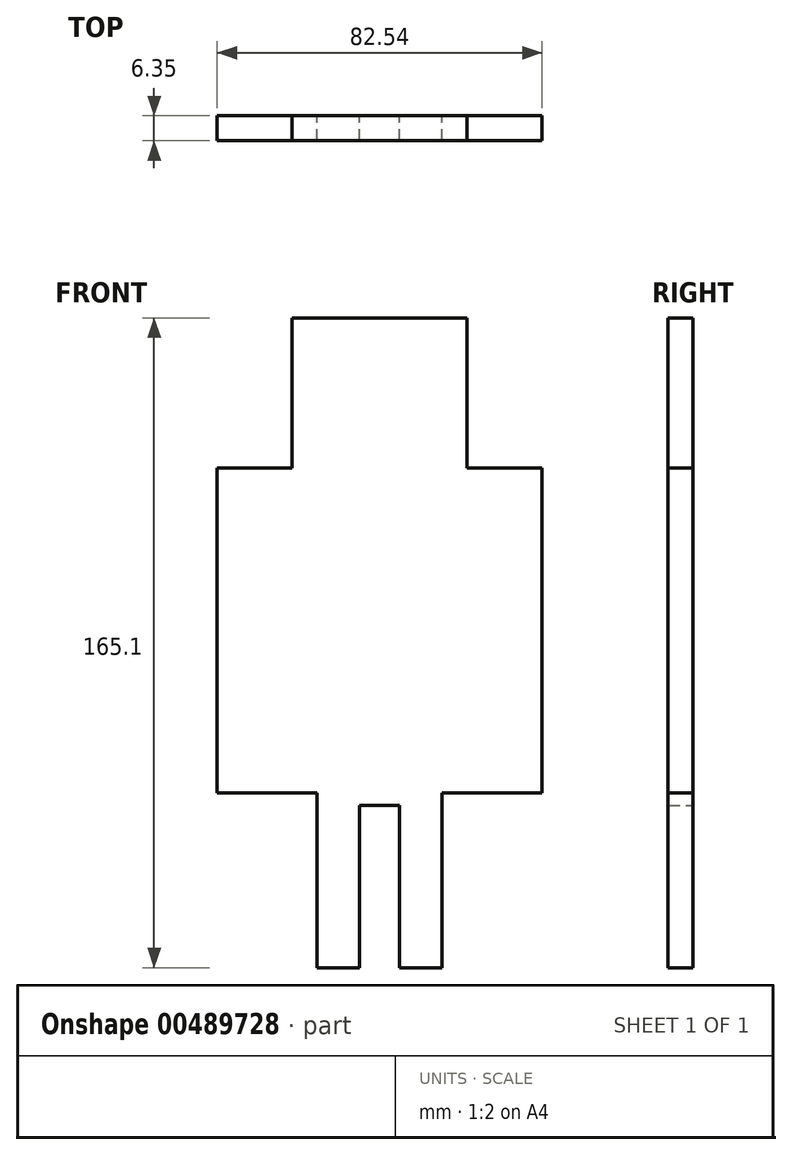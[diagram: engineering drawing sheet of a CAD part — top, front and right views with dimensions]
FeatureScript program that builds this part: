
annotation { "Feature Type Name" : "Feature", "Feature Type Description" : "" }
export const myFeature = defineFeature(function(context is Context, id is Id, definition is map)
    precondition{}
    {
        {
            var Q0;
            Q0=qCreatedBy(makeId("Front.planeOp"),FACE);
            var sketch = newSketch(context, id + "F0", { "sketchPlane" : qUnion([Q0])});
            skLineSegment(sketch, "E0.bottom", {"start": v(-22.23, 82.55) * mm, "end": v(22.23, 82.55) * mm});
            skLineSegment(sketch, "E0.top", {"start": v(-15.88, -82.55) * mm, "end": v(-5.08, -82.55) * mm});
            skLineSegment(sketch, "E0.left", {"start": v(-41.28, 44.45) * mm, "end": v(-41.28, -38.1) * mm});
            skLineSegment(sketch, "E0.right", {"start": v(41.28, 44.45) * mm, "end": v(41.28, -38.1) * mm});
            skLineSegment(sketch, "E1.bottom", {"start": v(-41.28, 44.45) * mm, "end": v(-41.28, 44.45) * mm});
            skLineSegment(sketch, "E2.MirrorCS", {"start": v(41.28, 44.45) * mm, "end": v(41.28, 44.45) * mm});
            skLineSegment(sketch, "E3.bottom", {"start": v(-41.28, -38.1) * mm, "end": v(-15.88, -38.1) * mm});
            skLineSegment(sketch, "E3.right", {"start": v(-15.88, -38.1) * mm, "end": v(-15.88, -82.55) * mm});
            skLineSegment(sketch, "E4.MirrorCS", {"start": v(41.28, -38.1) * mm, "end": v(15.88, -38.1) * mm});
            skLineSegment(sketch, "E5.MirrorCS", {"start": v(15.88, -38.1) * mm, "end": v(15.88, -82.55) * mm});
            skLineSegment(sketch, "E6.top", {"start": v(-5.08, -41.28) * mm, "end": v(5.08, -41.28) * mm});
            skLineSegment(sketch, "E6.left", {"start": v(-5.08, -82.55) * mm, "end": v(-5.08, -41.28) * mm});
            skLineSegment(sketch, "E6.right", {"start": v(5.08, -82.55) * mm, "end": v(5.08, -41.28) * mm});
            skLineSegment(sketch, "E7.trimOffspring", {"start": v(5.08, -82.55) * mm, "end": v(15.88, -82.55) * mm});
            skLineSegment(sketch, "E8.bottom", {"start": v(-41.28, 44.45) * mm, "end": v(-22.23, 44.45) * mm});
            skLineSegment(sketch, "E8.right", {"start": v(-22.23, 44.45) * mm, "end": v(-22.23, 82.55) * mm});
            skLineSegment(sketch, "E9.MirrorCS", {"start": v(41.28, 44.45) * mm, "end": v(22.23, 44.45) * mm});
            skLineSegment(sketch, "E10.MirrorCS", {"start": v(22.23, 44.45) * mm, "end": v(22.23, 82.55) * mm});
            skPoint(sketch, "E11.MirrorCS.start.orphan", {"position": v(41.28, 44.45) * mm});
            skSolve(sketch);
        }
        {
            var Q0;
            Q0 = qSketchRegion(id + "F0", true);
            extrude(context, id + "F1", {"entities" : qUnion([Q0]), "depth" : 6.35 * mm});
        }
    });
